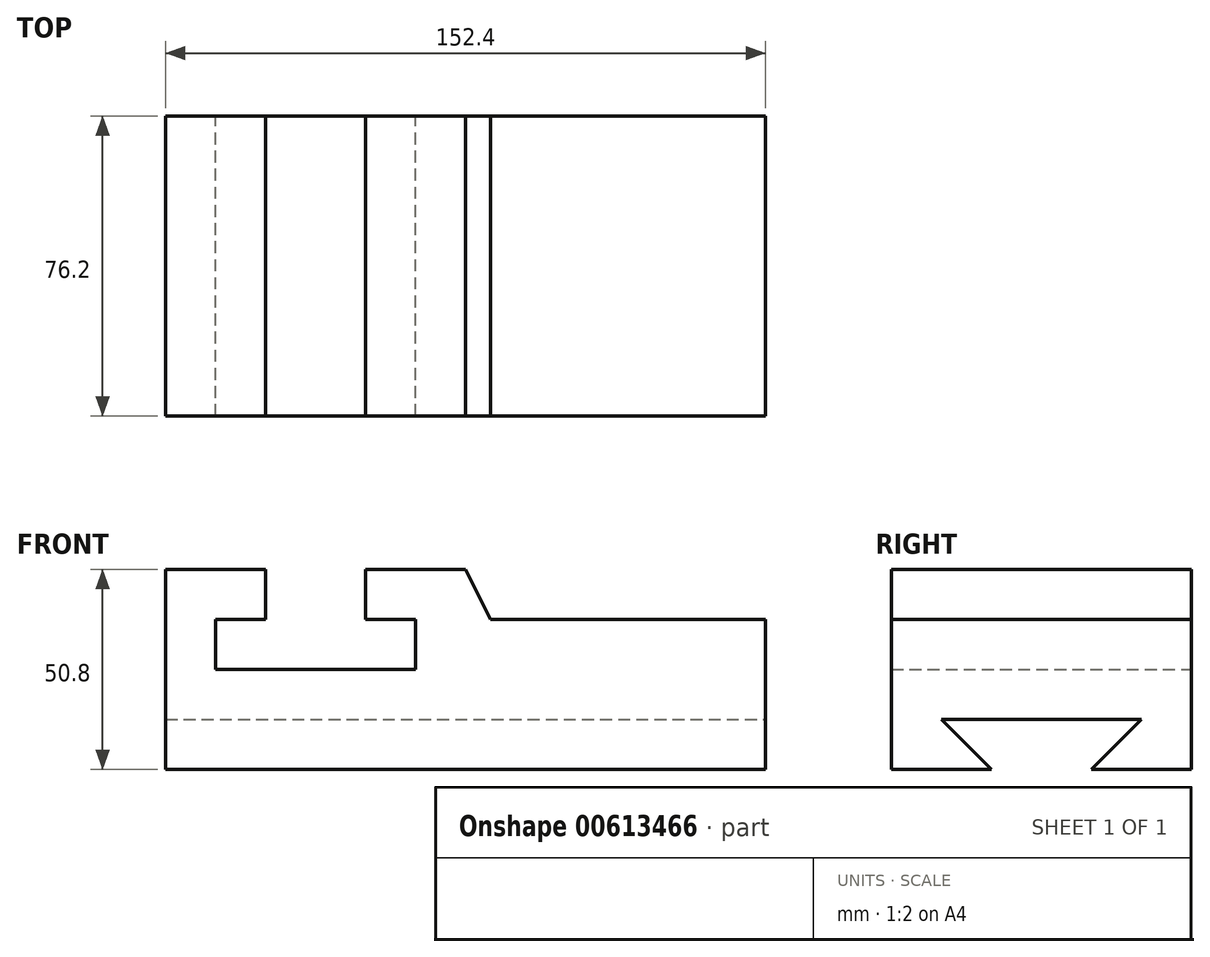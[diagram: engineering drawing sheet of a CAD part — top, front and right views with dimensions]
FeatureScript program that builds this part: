
annotation { "Feature Type Name" : "Feature", "Feature Type Description" : "" }
export const myFeature = defineFeature(function(context is Context, id is Id, definition is map)
    precondition{}
    {
        {
            var Q0;
            Q0=qCreatedBy(makeId("Front.planeOp"),FACE);
            var sketch = newSketch(context, id + "F0", { "sketchPlane" : qUnion([Q0])});
            skLineSegment(sketch, "E0", {"start": v(0, 0) * mm, "end": v(0, 50.8) * mm});
            skLineSegment(sketch, "E1", {"start": v(0, 50.8) * mm, "end": v(25.4, 50.8) * mm});
            skLineSegment(sketch, "E2", {"start": v(25.4, 50.8) * mm, "end": v(25.4, 38.1) * mm});
            skLineSegment(sketch, "E3", {"start": v(25.4, 38.1) * mm, "end": v(12.7, 38.1) * mm});
            skLineSegment(sketch, "E4", {"start": v(12.7, 38.1) * mm, "end": v(12.7, 25.4) * mm});
            skLineSegment(sketch, "E5", {"start": v(12.7, 25.4) * mm, "end": v(63.5, 25.4) * mm});
            skLineSegment(sketch, "E6", {"start": v(63.5, 25.4) * mm, "end": v(63.5, 38.1) * mm});
            skLineSegment(sketch, "E7", {"start": v(63.5, 38.1) * mm, "end": v(50.8, 38.1) * mm});
            skLineSegment(sketch, "E8", {"start": v(50.8, 38.1) * mm, "end": v(50.8, 50.8) * mm});
            skLineSegment(sketch, "E9", {"start": v(50.8, 50.8) * mm, "end": v(76.2, 50.8) * mm});
            skLineSegment(sketch, "E10", {"start": v(0, 0) * mm, "end": v(152.4, 0) * mm});
            skLineSegment(sketch, "E11", {"start": v(152.4, 0) * mm, "end": v(152.4, 38.1) * mm});
            skLineSegment(sketch, "E12", {"start": v(152.4, 38.1) * mm, "end": v(82.55, 38.1) * mm});
            skLineSegment(sketch, "E13", {"start": v(82.55, 38.1) * mm, "end": v(76.2, 50.8) * mm});
            skSolve(sketch);
        }
        {
            var Q0;
            Q0=makeQuery(id+"F0.imprint","IMPRINT",FACE,{"disambiguationData":[TD([[makeQuery(id+"F0.imprint","IMPRINT",EDGE,{"derivedFrom":sQuery(id+"F0.wireOp",EDGE,"E0")}),-1.0]])]});
            extrude(context, id + "F1", {"entities" : qUnion([Q0]), "depth" : 76.2 * mm, "offsetDistance" : 25.4 * mm});
        }
        {
            var Q0;
            Q0=makeQuery(id+"F1.opExtrude","SWEPT_FACE",FACE,{"disambiguationData":[OSD([sQuery(id+"F0.wireOp",EDGE,"E11")])]});
            var sketch = newSketch(context, id + "F2", { "sketchPlane" : qUnion([Q0])});
            skLineSegment(sketch, "E14", {"start": v(-76.2, 0) * mm, "end": v(-50.8, 0) * mm});
            skLineSegment(sketch, "E15", {"start": v(0, 0) * mm, "end": v(-25.4, 0) * mm});
            skLineSegment(sketch, "E16", {"start": v(-38.1, 0) * mm, "end": v(-38.1, 12.7) * mm});
            skLineSegment(sketch, "E17", {"start": v(-38.1, 12.7) * mm, "end": v(-12.7, 12.7) * mm});
            skLineSegment(sketch, "E18", {"start": v(-12.7, 12.7) * mm, "end": v(-63.5, 12.7) * mm});
            skLineSegment(sketch, "E19", {"start": v(-63.5, 12.7) * mm, "end": v(-50.8, 0) * mm});
            skLineSegment(sketch, "E20", {"start": v(-12.7, 12.7) * mm, "end": v(-25.4, 0) * mm});
            skSolve(sketch);
        }
        {
            var Q0;
            Q0 = qSketchRegion(id + "F2", true);
            var Q1;
            {var subQ0=sQuery(id+"F2.wireOp",EDGE,"E16");Q1=makeQuery(id+"F2.imprint","IMPRINT",FACE,{"disambiguationData":[TD([[makeQuery(id+"F2.imprint","IMPRINT",EDGE,{"derivedFrom":subQ0}),-1.0]])]});}
            var Q2;
            {var subQ0=sQuery(id+"F2.wireOp",EDGE,"E16");Q2=makeQuery(id+"F2.imprint","IMPRINT",FACE,{"disambiguationData":[TD([[makeQuery(id+"F2.imprint","IMPRINT",EDGE,{"derivedFrom":subQ0}),1.0]])]});}
            extrude(context, id + "F3", {"entities" : qUnion([Q0, Q1, Q2]), "operationType" : NewBodyOperationType.REMOVE, "oppositeDirection" : true, "depth" : 254 * mm, "offsetDistance" : 25.4 * mm});
        }
    });
